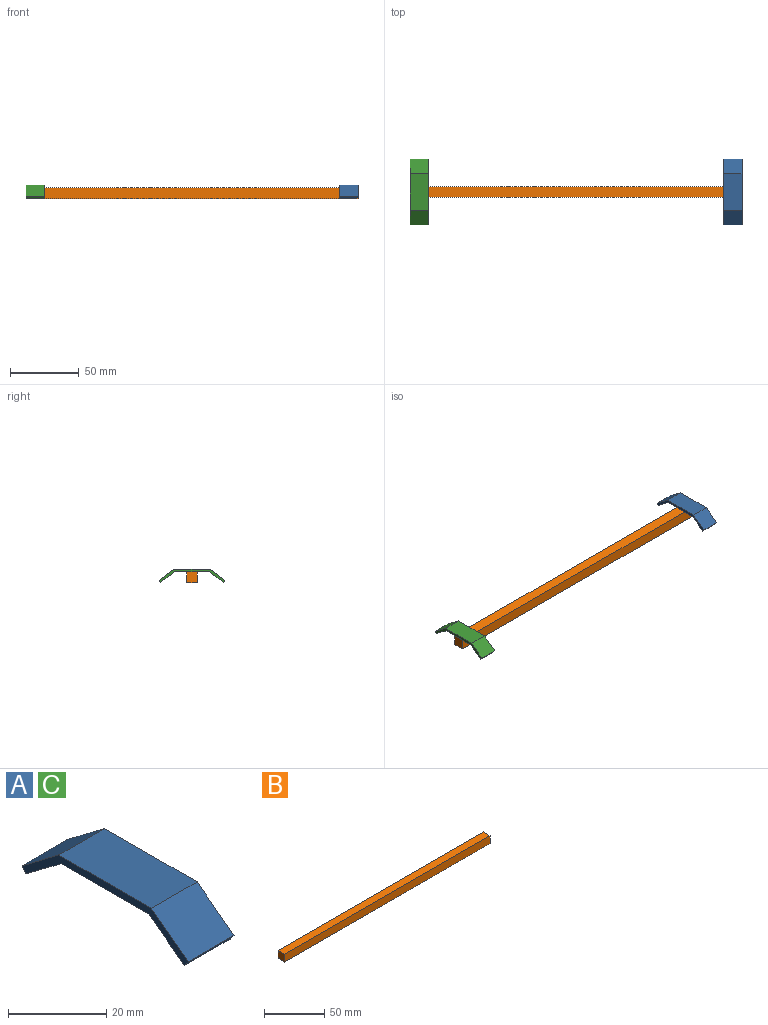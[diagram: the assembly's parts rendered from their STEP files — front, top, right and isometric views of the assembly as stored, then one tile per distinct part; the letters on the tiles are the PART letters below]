
ASSEMBLY  parts=3 mates=2
PART A: 10 faces, bbox 13.2x47.9x9.5 mm
  f0: plane 13.21x1.48mm, normal (0,-0.8,-0.6), area 24.5mm2, adj f1,f7,f8,f9
  f1: plane 13.21x10.14mm, normal (0,0.6,-0.8), area 167.7mm2, adj f0,f2,f8,f9
  f2: plane 25.4x13.21mm, normal (0,0,-1), area 335.5mm2, adj f1,f3,f8,f9
  f3: plane 13.21x10.14mm, normal (0,-0.6,-0.8), area 167.7mm2, adj f2,f4,f8,f9
  f4: plane 13.21x1.48mm, normal (0,0.8,-0.6), area 24.5mm2, adj f3,f5,f8,f9
  f5: plane 13.21x10.63mm, normal (0,0.6,0.8), area 175.9mm2, adj f4,f6,f8,f9
  f6: plane 26.64x13.21mm, normal (0,0,1), area 351.9mm2, adj f5,f7,f8,f9
  f7: plane 13.21x10.63mm, normal (0,-0.6,0.8), area 175.9mm2, adj f0,f6,f8,f9
  f8: plane 47.91x9.5mm, normal (1,0,0), area 96.5mm2, adj f0,f1,f2,f3,f4,f5,f6,f7
  f9: plane 47.91x9.5mm, normal (-1,0,0), area 96.5mm2, adj f0,f1,f2,f3,f4,f5,f6,f7
PART B: 6 faces, bbox 241.3x7.9x7.9 mm
  f0: plane 241.3x7.94mm, normal (0,0,-1), area 1915.3mm2, adj f1,f3,f4,f5
  f1: plane 241.3x7.94mm, normal (0,1,0), area 1915.3mm2, adj f0,f2,f4,f5
  f2: plane 241.3x7.94mm, normal (0,0,1), area 1915.3mm2, adj f1,f3,f4,f5
  f3: plane 241.3x7.94mm, normal (0,-1,0), area 1915.3mm2, adj f0,f2,f4,f5
  f4: plane 7.94x7.94mm, normal (1,0,0), area 63mm2, adj f0,f1,f2,f3
  f5: plane 7.94x7.94mm, normal (-1,0,0), area 63mm2, adj f0,f1,f2,f3
PART C: same geometry as A
PLACE A t=(850.22,353.33,-93.67)mm
PLACE B t=(736.18,353.33,-98.57)mm
PLACE C t=(622.13,353.33,-93.67)mm
MATE fastened A.f2 <-> B.f2  axis (0,0,-1) through (856.83,353.33,-94.6)mm
MATE fastened C.f2 <-> B.f2  axis (0,0,-1) through (615.53,353.33,-94.6)mm
